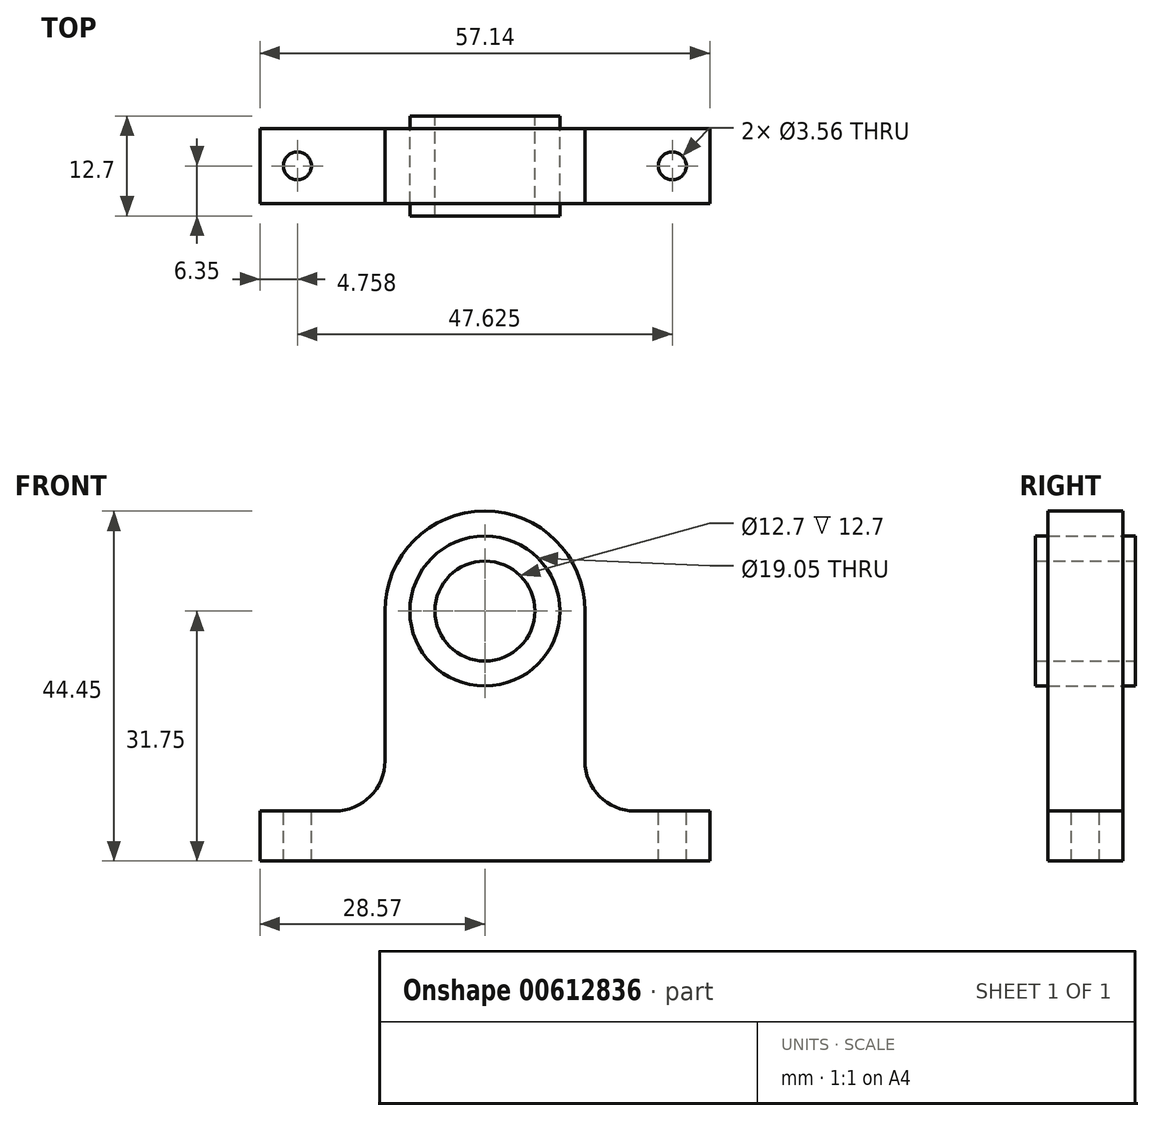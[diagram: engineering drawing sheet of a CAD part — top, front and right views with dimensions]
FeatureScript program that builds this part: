
annotation { "Feature Type Name" : "Feature", "Feature Type Description" : "" }
export const myFeature = defineFeature(function(context is Context, id is Id, definition is map)
    precondition{}
    {
        {
            var Q0;
            Q0=qCreatedBy(makeId("Front.planeOp"),FACE);
            var sketch = newSketch(context, id + "F0", { "sketchPlane" : qUnion([Q0])});
            skArc(sketch, "E0", {"start": v(-12.7, 0) * mm, "mid": v(0, 12.7) * mm, "end": v(12.7, 0) * mm});
            skLineSegment(sketch, "E1", {"start": v(-12.7, 0) * mm, "end": v(-12.7, -19.05) * mm});
            skLineSegment(sketch, "E2", {"start": v(-19.05, -25.4) * mm, "end": v(-28.58, -25.4) * mm});
            skLineSegment(sketch, "E3", {"start": v(-28.58, -25.4) * mm, "end": v(-28.58, -31.75) * mm});
            skLineSegment(sketch, "E4", {"start": v(-28.58, -31.75) * mm, "end": v(28.58, -31.75) * mm});
            skLineSegment(sketch, "E5", {"start": v(28.57, -31.75) * mm, "end": v(28.57, -25.4) * mm});
            skLineSegment(sketch, "E6", {"start": v(28.58, -25.4) * mm, "end": v(19.05, -25.4) * mm});
            skLineSegment(sketch, "E7", {"start": v(12.7, -19.05) * mm, "end": v(12.7, 0) * mm});
            skCircle(sketch, "E8", {"center": v(0, 0) * mm, "radius": 9.53 * mm});
            skPoint(sketch, "E9", {"position": v(0, -31.75) * mm});
            skPoint(sketch, "E10.visualSharp", {"position": v(-12.7, -25.4) * mm});
            skArc(sketch, "E10.filletArc", {"start": v(-19.05, -25.4) * mm, "mid": v(-14.56, -23.54) * mm, "end": v(-12.7, -19.05) * mm});
            skPoint(sketch, "E11.visualSharp", {"position": v(12.7, -25.4) * mm});
            skArc(sketch, "E11.filletArc", {"start": v(12.7, -19.05) * mm, "mid": v(14.56, -23.54) * mm, "end": v(19.05, -25.4) * mm});
            skSolve(sketch);
        }
        {
            var Q0;
            Q0=qSketchRegion(id+"F0",true);
            extrude(context, id + "F1", {"entities" : qUnion([Q0]), "depth" : 9.52 * mm, "symmetric" : true});
        }
        {
            var Q0;
            Q0=makeQuery(id+"F1.opExtrude","SWEPT_FACE",FACE,{"disambiguationData":[OSD([sQuery(id+"F0.wireOp",EDGE,"E4")])]});
            var sketch = newSketch(context, id + "F2", { "sketchPlane" : qUnion([Q0])});
            skPoint(sketch, "E12", {"position": v(23.81, 0) * mm});
            skPoint(sketch, "E13", {"position": v(-23.81, 0) * mm});
            skSolve(sketch);
        }
        {
            var Q0;
            Q0=sQuery(id+"F2.wireOp",VERTEX,"E13");
            var Q1;
            Q1=sQuery(id+"F2.wireOp",VERTEX,"E12");
            var Q2;
            Q2=makeQuery(id+"F1.opExtrude","SWEPT_BODY",BODY,{"disambiguationData":[OSD([sQuery(id+"F0.wireOp",EDGE,"E0"),sQuery(id+"F0.wireOp",EDGE,"E1"),sQuery(id+"F0.wireOp",EDGE,"E2"),sQuery(id+"F0.wireOp",EDGE,"E3"),sQuery(id+"F0.wireOp",EDGE,"E4"),sQuery(id+"F0.wireOp",EDGE,"E5"),sQuery(id+"F0.wireOp",EDGE,"E6"),sQuery(id+"F0.wireOp",EDGE,"E7"),sQuery(id+"F0.wireOp",EDGE,"E8"),sQuery(id+"F0.wireOp",EDGE,"E10.filletArc"),sQuery(id+"F0.wireOp",EDGE,"E11.filletArc")])]});
            hole(context, id + "F3", {"style" : HoleStyle.SIMPLE, "holeDiameter" : 3.56 * mm, "endStyle" : HoleEndStyle.THROUGH, "locations" : qUnion([Q0, Q1]), "scope" : qUnion([Q2])});
        }
        {
            var Q0;
            Q0=qCreatedBy(makeId("Front.planeOp"),FACE);
            var sketch = newSketch(context, id + "F4", { "sketchPlane" : qUnion([Q0])});
            skCircle(sketch, "E14", {"center": v(0, 0) * mm, "radius": 9.53 * mm});
            skCircle(sketch, "E15", {"center": v(0, 0) * mm, "radius": 6.35 * mm});
            skSolve(sketch);
        }
        {
            var Q0;
            Q0=qSketchRegion(id+"F4",true);
            extrude(context, id + "F5", {"entities" : qUnion([Q0]), "depth" : 12.7 * mm, "symmetric" : true});
        }
    });
